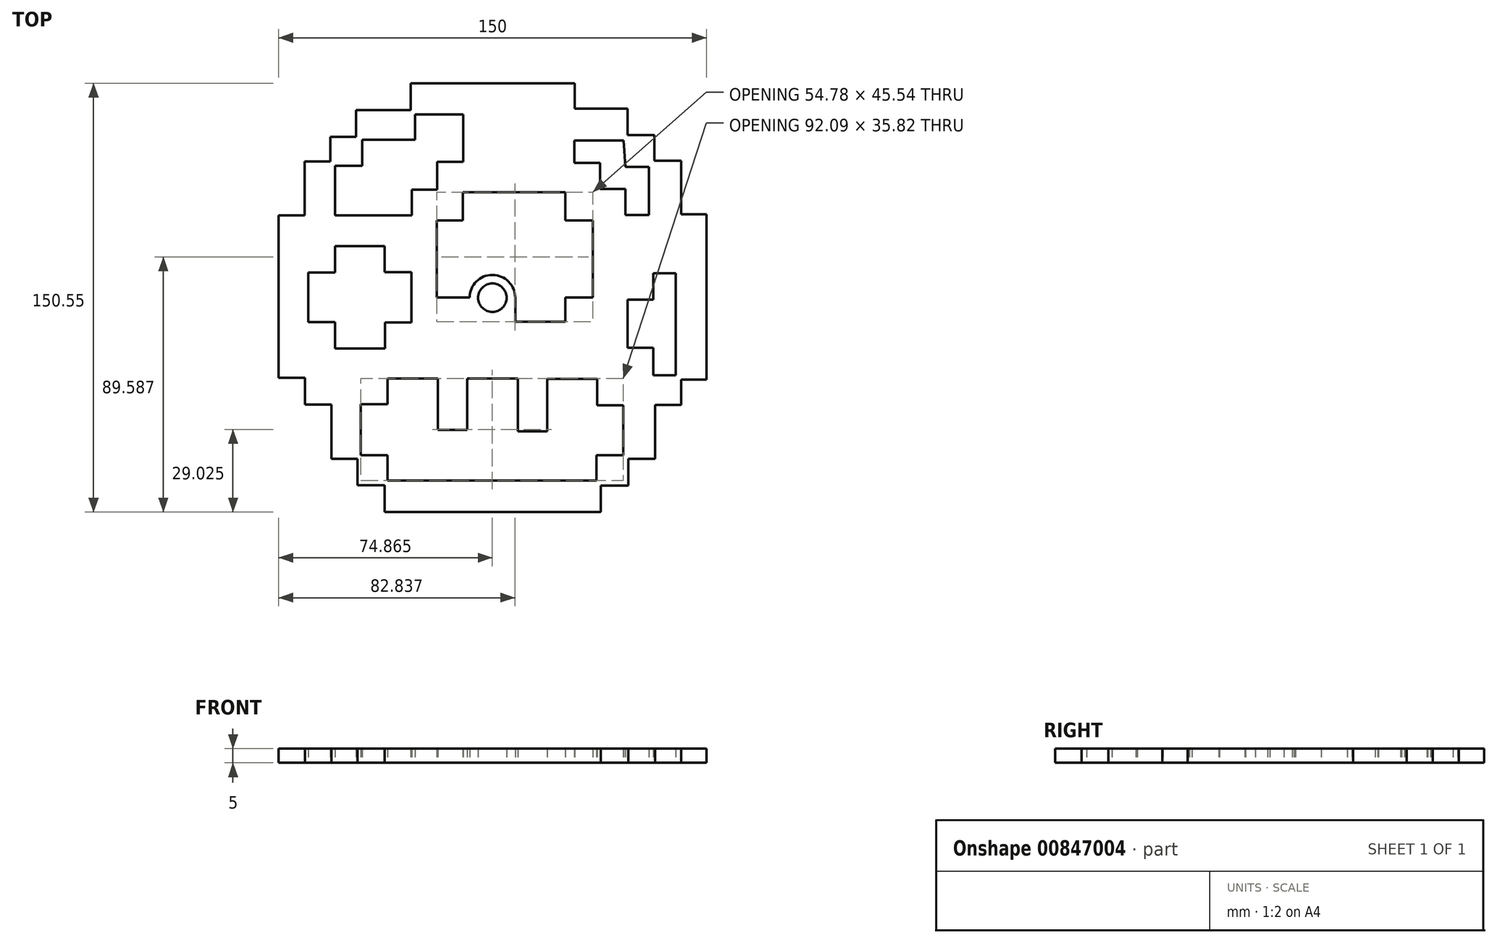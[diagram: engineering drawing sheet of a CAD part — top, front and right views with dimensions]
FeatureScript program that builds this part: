
annotation { "Feature Type Name" : "Feature", "Feature Type Description" : "" }
export const myFeature = defineFeature(function(context is Context, id is Id, definition is map)
    precondition{}
    {
        {
            var Q0;
            Q0=qCreatedBy(makeId("Top.planeOp"),FACE);
            var sketch = newSketch(context, id + "F0", { "sketchPlane" : qUnion([Q0])});
            skLineSegment(sketch, "E0", {"start": v(28.84, 75.26) * mm, "end": v(28.84, 66.32) * mm});
            skLineSegment(sketch, "E1", {"start": v(28.84, 66.32) * mm, "end": v(47.47, 66.32) * mm});
            skLineSegment(sketch, "E2", {"start": v(47.47, 66.32) * mm, "end": v(47.47, 57.16) * mm});
            skLineSegment(sketch, "E3", {"start": v(47.47, 57.16) * mm, "end": v(56.76, 57.16) * mm});
            skLineSegment(sketch, "E4", {"start": v(56.76, 57.16) * mm, "end": v(56.76, 48.02) * mm});
            skLineSegment(sketch, "E5", {"start": v(56.76, 48.02) * mm, "end": v(66.2, 48.02) * mm});
            skLineSegment(sketch, "E6", {"start": v(66.2, 48.02) * mm, "end": v(66.2, 29.31) * mm});
            skLineSegment(sketch, "E7", {"start": v(66.2, 29.31) * mm, "end": v(75.04, 29.31) * mm});
            skLineSegment(sketch, "E8", {"start": v(28.72, 55.17) * mm, "end": v(46.07, 55.17) * mm});
            skLineSegment(sketch, "E9", {"start": v(46.07, 55.17) * mm, "end": v(46.7, 45.9) * mm});
            skLineSegment(sketch, "E10", {"start": v(46.7, 45.9) * mm, "end": v(54.88, 45.9) * mm});
            skLineSegment(sketch, "E11", {"start": v(54.88, 45.9) * mm, "end": v(54.88, 29.09) * mm});
            skLineSegment(sketch, "E12", {"start": v(54.88, 29.09) * mm, "end": v(46.7, 29.09) * mm});
            skLineSegment(sketch, "E13", {"start": v(46.7, 29.09) * mm, "end": v(46.7, 38.14) * mm});
            skLineSegment(sketch, "E14", {"start": v(46.7, 38.14) * mm, "end": v(37.83, 38.14) * mm});
            skLineSegment(sketch, "E15", {"start": v(37.83, 38.14) * mm, "end": v(37.83, 47.34) * mm});
            skLineSegment(sketch, "E16", {"start": v(37.83, 47.34) * mm, "end": v(28.72, 47.34) * mm});
            skLineSegment(sketch, "E17", {"start": v(28.72, 47.34) * mm, "end": v(28.72, 55.17) * mm});
            skLineSegment(sketch, "E18.bottom", {"start": v(64.25, 8.55) * mm, "end": v(64.25, -27.21) * mm});
            skLineSegment(sketch, "E18.top", {"start": v(56.48, 8.55) * mm, "end": v(56.48, -0.68) * mm});
            skLineSegment(sketch, "E18.left", {"start": v(64.25, 8.55) * mm, "end": v(56.48, 8.55) * mm});
            skLineSegment(sketch, "E18.right", {"start": v(64.25, -27.21) * mm, "end": v(56.48, -27.21) * mm});
            skLineSegment(sketch, "E19.left", {"start": v(56.48, -17.53) * mm, "end": v(47.4, -17.53) * mm});
            skLineSegment(sketch, "E20.trimOffspring", {"start": v(56.48, -17.53) * mm, "end": v(56.48, -27.21) * mm});
            skLineSegment(sketch, "E21.bottom", {"start": v(35.27, 27.19) * mm, "end": v(35.27, 0.07) * mm});
            skLineSegment(sketch, "E21.top", {"start": v(-19.51, 27.19) * mm, "end": v(-19.51, 0.07) * mm});
            skLineSegment(sketch, "E22.left", {"start": v(-10.31, -8.47) * mm, "end": v(25.6, -8.47) * mm});
            skLineSegment(sketch, "E22.right", {"start": v(-10.31, 37.07) * mm, "end": v(25.6, 37.07) * mm});
            skLineSegment(sketch, "E23.bottom", {"start": v(-10.26, 64.31) * mm, "end": v(-10.26, 47.71) * mm});
            skLineSegment(sketch, "E23.left", {"start": v(-10.26, 64.31) * mm, "end": v(-27.16, 64.31) * mm});
            skLineSegment(sketch, "E24.top", {"start": v(-55.2, 28.94) * mm, "end": v(-55.2, 46.32) * mm});
            skLineSegment(sketch, "E24.left", {"start": v(-28.33, 28.94) * mm, "end": v(-55.2, 28.94) * mm});
            skLineSegment(sketch, "E25.bottom", {"start": v(-28.38, 9.02) * mm, "end": v(-28.38, -8.73) * mm});
            skLineSegment(sketch, "E25.top", {"start": v(-64.6, 8.78) * mm, "end": v(-64.6, -8.57) * mm});
            skLineSegment(sketch, "E26.left", {"start": v(-55.2, -17.88) * mm, "end": v(-37.61, -17.88) * mm});
            skLineSegment(sketch, "E26.right", {"start": v(-55.2, 18.09) * mm, "end": v(-37.77, 18.09) * mm});
            skLineSegment(sketch, "E27.left", {"start": v(36.72, -28.53) * mm, "end": v(19.26, -28.53) * mm});
            skLineSegment(sketch, "E28.top", {"start": v(45.95, -37.75) * mm, "end": v(45.95, -55.26) * mm});
            skLineSegment(sketch, "E28.left", {"start": v(36.72, -37.75) * mm, "end": v(45.95, -37.75) * mm});
            skLineSegment(sketch, "E28.right", {"start": v(36.5, -55.26) * mm, "end": v(45.95, -55.26) * mm});
            skLineSegment(sketch, "E29.bottom", {"start": v(8.9, -28.36) * mm, "end": v(8.9, -46.92) * mm});
            skLineSegment(sketch, "E29.top", {"start": v(-8.8, -28.36) * mm, "end": v(-8.8, -46.44) * mm});
            skLineSegment(sketch, "E29.left", {"start": v(8.9, -28.36) * mm, "end": v(-8.8, -28.36) * mm});
            skLineSegment(sketch, "E30.left", {"start": v(-36.74, -28.37) * mm, "end": v(-19.17, -28.37) * mm});
            skLineSegment(sketch, "E31.bottom", {"start": v(-46.14, -37.37) * mm, "end": v(-46.14, -55.28) * mm});
            skLineSegment(sketch, "E31.left", {"start": v(-46.14, -37.37) * mm, "end": v(-36.74, -37.37) * mm});
            skLineSegment(sketch, "E31.right", {"start": v(-46.14, -55.28) * mm, "end": v(-36.74, -55.28) * mm});
            skLineSegment(sketch, "E32.left", {"start": v(75.04, -28.78) * mm, "end": v(66.21, -28.78) * mm});
            skLineSegment(sketch, "E33.left", {"start": v(66.21, -37.61) * mm, "end": v(57.02, -37.61) * mm});
            skLineSegment(sketch, "E34.left", {"start": v(57.02, -56.53) * mm, "end": v(47.7, -56.53) * mm});
            skLineSegment(sketch, "E35.top", {"start": v(38.07, -65.97) * mm, "end": v(38.07, -75.3) * mm});
            skLineSegment(sketch, "E35.left", {"start": v(47.7, -65.97) * mm, "end": v(38.07, -65.97) * mm});
            skLineSegment(sketch, "E36.bottom", {"start": v(-37.76, -65.85) * mm, "end": v(-37.76, -75.3) * mm});
            skLineSegment(sketch, "E37.bottom", {"start": v(-47.3, -56.55) * mm, "end": v(-47.3, -65.85) * mm});
            skLineSegment(sketch, "E38.bottom", {"start": v(-56.4, -37.47) * mm, "end": v(-56.4, -56.55) * mm});
            skLineSegment(sketch, "E39.bottom", {"start": v(-65.7, -28.07) * mm, "end": v(-65.7, -37.47) * mm});
            skLineSegment(sketch, "E39.left", {"start": v(-65.7, -28.07) * mm, "end": v(-74.96, -28.07) * mm});
            skLineSegment(sketch, "E40.left", {"start": v(-74.96, 28.91) * mm, "end": v(-65.81, 28.91) * mm});
            skLineSegment(sketch, "E41.left", {"start": v(-65.81, 47.77) * mm, "end": v(-56.84, 47.77) * mm});
            skLineSegment(sketch, "E42.left", {"start": v(-56.84, 56.48) * mm, "end": v(-47.8, 56.48) * mm});
            skLineSegment(sketch, "E43.top", {"start": v(-28.63, 65.92) * mm, "end": v(-28.63, 75.26) * mm});
            skLineSegment(sketch, "E43.left", {"start": v(-47.8, 65.92) * mm, "end": v(-28.63, 65.92) * mm});
            skLineSegment(sketch, "E44", {"start": v(-19.51, 27.19) * mm, "end": v(-10.31, 27.19) * mm});
            skLineSegment(sketch, "E45", {"start": v(35.27, 27.19) * mm, "end": v(25.6, 27.19) * mm});
            skLineSegment(sketch, "E46", {"start": v(-19.51, 0.07) * mm, "end": v(-10.31, 0.07) * mm});
            skLineSegment(sketch, "E47", {"start": v(35.27, 0.07) * mm, "end": v(25.6, 0.07) * mm});
            skLineSegment(sketch, "E48", {"start": v(25.6, -8.47) * mm, "end": v(25.6, 0.07) * mm});
            skLineSegment(sketch, "E49", {"start": v(25.6, 27.19) * mm, "end": v(25.6, 37.07) * mm});
            skLineSegment(sketch, "E50", {"start": v(-10.31, 27.19) * mm, "end": v(-10.31, 37.07) * mm});
            skLineSegment(sketch, "E51", {"start": v(-10.31, 0.07) * mm, "end": v(-10.31, -8.47) * mm});
            skLineSegment(sketch, "E52", {"start": v(66.21, -28.78) * mm, "end": v(66.21, -37.61) * mm});
            skLineSegment(sketch, "E53", {"start": v(57.02, -37.61) * mm, "end": v(57.02, -56.53) * mm});
            skLineSegment(sketch, "E54", {"start": v(47.7, -56.53) * mm, "end": v(47.7, -65.97) * mm});
            skLineSegment(sketch, "E55", {"start": v(38.07, -75.3) * mm, "end": v(-37.76, -75.3) * mm});
            skLineSegment(sketch, "E56", {"start": v(-47.3, -65.85) * mm, "end": v(-37.76, -65.85) * mm});
            skLineSegment(sketch, "E57", {"start": v(-47.3, -56.55) * mm, "end": v(-56.4, -56.55) * mm});
            skLineSegment(sketch, "E58", {"start": v(-56.4, -37.47) * mm, "end": v(-65.7, -37.47) * mm});
            skLineSegment(sketch, "E59", {"start": v(-74.96, -28.07) * mm, "end": v(-74.96, 28.91) * mm});
            skLineSegment(sketch, "E60", {"start": v(-65.81, 28.91) * mm, "end": v(-65.81, 47.77) * mm});
            skLineSegment(sketch, "E61", {"start": v(-56.84, 47.77) * mm, "end": v(-56.84, 56.48) * mm});
            skLineSegment(sketch, "E62", {"start": v(-47.8, 56.48) * mm, "end": v(-47.8, 65.92) * mm});
            skLineSegment(sketch, "E63", {"start": v(-27.16, 64.31) * mm, "end": v(-27.16, 55.47) * mm});
            skLineSegment(sketch, "E64", {"start": v(-27.16, 55.47) * mm, "end": v(-45.66, 55.47) * mm});
            skLineSegment(sketch, "E65", {"start": v(-45.66, 55.47) * mm, "end": v(-45.66, 46.32) * mm});
            skLineSegment(sketch, "E66", {"start": v(-45.66, 46.32) * mm, "end": v(-55.2, 46.32) * mm});
            skLineSegment(sketch, "E67", {"start": v(-28.33, 28.94) * mm, "end": v(-28.33, 37.9) * mm});
            skLineSegment(sketch, "E68", {"start": v(-28.33, 37.9) * mm, "end": v(-19.32, 37.9) * mm});
            skLineSegment(sketch, "E69", {"start": v(-28.63, 75.26) * mm, "end": v(28.84, 75.26) * mm});
            skLineSegment(sketch, "E70", {"start": v(-37.77, 18.09) * mm, "end": v(-37.77, 9.02) * mm});
            skLineSegment(sketch, "E71", {"start": v(-37.77, 9.02) * mm, "end": v(-28.38, 9.02) * mm});
            skLineSegment(sketch, "E72", {"start": v(-28.38, -8.73) * mm, "end": v(-37.61, -8.73) * mm});
            skLineSegment(sketch, "E73", {"start": v(-37.61, -8.73) * mm, "end": v(-37.61, -17.88) * mm});
            skLineSegment(sketch, "E74", {"start": v(-55.2, -17.88) * mm, "end": v(-55.2, -8.57) * mm});
            skLineSegment(sketch, "E75", {"start": v(-64.6, -8.57) * mm, "end": v(-55.2, -8.57) * mm});
            skLineSegment(sketch, "E76", {"start": v(-64.6, 8.78) * mm, "end": v(-55.2, 8.78) * mm});
            skLineSegment(sketch, "E77", {"start": v(-55.2, 8.78) * mm, "end": v(-55.2, 18.09) * mm});
            skLineSegment(sketch, "E78", {"start": v(-36.74, -55.28) * mm, "end": v(-36.74, -64.17) * mm});
            skLineSegment(sketch, "E79", {"start": v(-36.74, -37.37) * mm, "end": v(-36.74, -28.37) * mm});
            skLineSegment(sketch, "E80", {"start": v(-19.17, -28.37) * mm, "end": v(-19.17, -46.44) * mm});
            skLineSegment(sketch, "E81", {"start": v(-19.17, -46.44) * mm, "end": v(-8.8, -46.44) * mm});
            skLineSegment(sketch, "E82", {"start": v(8.9, -46.92) * mm, "end": v(19.26, -46.92) * mm});
            skLineSegment(sketch, "E83", {"start": v(19.26, -46.92) * mm, "end": v(19.26, -28.53) * mm});
            skLineSegment(sketch, "E84", {"start": v(36.72, -28.53) * mm, "end": v(36.72, -37.75) * mm});
            skLineSegment(sketch, "E85", {"start": v(36.5, -55.26) * mm, "end": v(36.5, -64.17) * mm});
            skLineSegment(sketch, "E86", {"start": v(-36.74, -64.17) * mm, "end": v(36.5, -64.17) * mm});
            skLineSegment(sketch, "E87", {"start": v(75.04, 29.31) * mm, "end": v(75.04, -28.78) * mm});
            skLineSegment(sketch, "E88", {"start": v(56.48, -0.68) * mm, "end": v(47.47, -0.68) * mm});
            skLineSegment(sketch, "E89", {"start": v(47.47, -0.68) * mm, "end": v(47.4, -17.53) * mm});
            skLineSegment(sketch, "E90", {"start": v(-19.32, 37.9) * mm, "end": v(-19.32, 47.71) * mm});
            skLineSegment(sketch, "E91", {"start": v(-19.32, 47.71) * mm, "end": v(-10.26, 47.71) * mm});
            skCircle(sketch, "E92", {"center": v(0, 0) * mm, "radius": 8 * mm});
            skCircle(sketch, "E93.0", {"center": v(0, 0) * mm, "radius": 5 * mm});
            skLineSegment(sketch, "E94", {"start": v(-10.31, 0.07) * mm, "end": v(-8, 0.07) * mm});
            skLineSegment(sketch, "E95", {"start": v(8, 0) * mm, "end": v(8, -8.47) * mm});
            skPoint(sketch, "E96.center", {"position": v(1.03, 1.97) * mm});
            skSolve(sketch);
        }
        {
            var Q0;
            {var subQ47=sQuery(id+"F0.wireOp",EDGE,"E0");Q0=makeQuery(id+"F0.imprint","IMPRINT",FACE,{"disambiguationData":[TD([[makeQuery(id+"F0.imprint","IMPRINT",EDGE,{"derivedFrom":subQ47}),-1.0]])]});}
            var Q1;
            {var subQ5=sQuery(id+"F0.wireOp",EDGE,"E96.1.2");Q1=makeQuery(id+"F0.imprint","IMPRINT",FACE,{"disambiguationData":[TD([[makeQuery(id+"F0.imprint","IMPRINT",EDGE,{"derivedFrom":subQ5}),1.0]])]});}
            var Q2;
            {var subQ5=sQuery(id+"F0.wireOp",EDGE,"E96.1.0");Q2=makeQuery(id+"F0.imprint","IMPRINT",FACE,{"disambiguationData":[TD([[makeQuery(id+"F0.imprint","IMPRINT",EDGE,{"derivedFrom":subQ5}),-1.0]])]});}
            var Q3;
            {var subQ5=sQuery(id+"F0.wireOp",EDGE,"E96.2.2");Q3=makeQuery(id+"F0.imprint","IMPRINT",FACE,{"disambiguationData":[TD([[makeQuery(id+"F0.imprint","IMPRINT",EDGE,{"derivedFrom":subQ5}),1.0]])]});}
            var Q4;
            {var subQ5=sQuery(id+"F0.wireOp",EDGE,"E96.2.0");Q4=makeQuery(id+"F0.imprint","IMPRINT",FACE,{"disambiguationData":[TD([[makeQuery(id+"F0.imprint","IMPRINT",EDGE,{"derivedFrom":subQ5}),-1.0]])]});}
            var Q5;
            {var subQ5=sQuery(id+"F0.wireOp",EDGE,"E96.3.2");Q5=makeQuery(id+"F0.imprint","IMPRINT",FACE,{"disambiguationData":[TD([[makeQuery(id+"F0.imprint","IMPRINT",EDGE,{"derivedFrom":subQ5}),1.0]])]});}
            var Q6;
            {var subQ5=sQuery(id+"F0.wireOp",EDGE,"E96.3.0");Q6=makeQuery(id+"F0.imprint","IMPRINT",FACE,{"disambiguationData":[TD([[makeQuery(id+"F0.imprint","IMPRINT",EDGE,{"derivedFrom":subQ5}),-1.0]])]});}
            var Q7;
            {var subQ0=sQuery(id+"F0.wireOp",EDGE,"b5d18da8-e20b-45f5-a40c-556fc24cc88c.4.4.0");Q7=makeQuery(id+"F0.imprint","IMPRINT",FACE,{"disambiguationData":[TD([[makeQuery(id+"F0.imprint","IMPRINT",EDGE,{"derivedFrom":subQ0}),-1.0]])]});}
            var Q8;
            {var subQ0=sQuery(id+"F0.wireOp",EDGE,"b5d18da8-e20b-45f5-a40c-556fc24cc88c.6.4.0");Q8=makeQuery(id+"F0.imprint","IMPRINT",FACE,{"disambiguationData":[TD([[makeQuery(id+"F0.imprint","IMPRINT",EDGE,{"derivedFrom":subQ0}),1.0]])]});}
            var Q9;
            {var subQ0=sQuery(id+"F0.wireOp",EDGE,"b5d18da8-e20b-45f5-a40c-556fc24cc88c.6.5.0");Q9=makeQuery(id+"F0.imprint","IMPRINT",FACE,{"disambiguationData":[TD([[makeQuery(id+"F0.imprint","IMPRINT",EDGE,{"derivedFrom":subQ0}),1.0]])]});}
            var Q10;
            {var subQ0=sQuery(id+"F0.wireOp",EDGE,"E56");var subQ1=sQuery(id+"F0.wireOp",EDGE,"E36.bottom");var subQ2=makeQuery(id+"F0.imprint","INTERSECT",VERTEX,{"derivedFrom":[subQ1,subQ0]});Q10=makeQuery(id+"F0.imprint","IMPRINT",FACE,{"disambiguationData":[TD([[makeQuery(id+"F0.imprint","IMPRINT",EDGE,{"disambiguationData":[TD([[subQ2,-1.0]])],"derivedFrom":subQ1}),-1.0]])]});}
            var Q11;
            {var subQ5=sQuery(id+"F0.wireOp",EDGE,"b5d18da8-e20b-45f5-a40c-556fc24cc88c.4.6.0");Q11=makeQuery(id+"F0.imprint","IMPRINT",FACE,{"disambiguationData":[TD([[makeQuery(id+"F0.imprint","IMPRINT",EDGE,{"derivedFrom":subQ5}),-1.0]])]});}
            var Q12;
            {var subQ15=sQuery(id+"F0.wireOp",EDGE,"E35.top");Q12=makeQuery(id+"F0.imprint","IMPRINT",FACE,{"disambiguationData":[TD([[makeQuery(id+"F0.imprint","IMPRINT",EDGE,{"derivedFrom":subQ15}),-1.0]])]});}
            var Q13;
            {var subQ5=sQuery(id+"F0.wireOp",EDGE,"b5d18da8-e20b-45f5-a40c-556fc24cc88c.6.6.0");Q13=makeQuery(id+"F0.imprint","IMPRINT",FACE,{"disambiguationData":[TD([[makeQuery(id+"F0.imprint","IMPRINT",EDGE,{"derivedFrom":subQ5}),1.0]])]});}
            var Q14;
            {var subQ7=sQuery(id+"F0.wireOp",EDGE,"E56");var subQ8=sQuery(id+"F0.wireOp",EDGE,"E36.bottom");var subQ9=makeQuery(id+"F0.imprint","INTERSECT",VERTEX,{"derivedFrom":[subQ8,subQ7]});Q14=makeQuery(id+"F0.imprint","IMPRINT",FACE,{"disambiguationData":[TD([[makeQuery(id+"F0.imprint","IMPRINT",EDGE,{"disambiguationData":[TD([[subQ9,-1.0]])],"derivedFrom":subQ8}),1.0]])]});}
            var Q15;
            {var subQ3=sQuery(id+"F0.wireOp",EDGE,"E28.right");var subQ7=sQuery(id+"F0.wireOp",EDGE,"b5d18da8-e20b-45f5-a40c-556fc24cc88c.6.7.0");var subQ11=makeQuery(id+"F0.imprint","INTERSECT",VERTEX,{"derivedFrom":[subQ3,subQ7]});Q15=makeQuery(id+"F0.imprint","IMPRINT",FACE,{"disambiguationData":[TD([[makeQuery(id+"F0.imprint","IMPRINT",EDGE,{"disambiguationData":[TD([[subQ11,-1.0]])],"derivedFrom":subQ3}),-1.0]])]});}
            var Q16;
            {var subQ5=sQuery(id+"F0.wireOp",EDGE,"b5d18da8-e20b-45f5-a40c-556fc24cc88c.4.7.0");Q16=makeQuery(id+"F0.imprint","IMPRINT",FACE,{"disambiguationData":[TD([[makeQuery(id+"F0.imprint","IMPRINT",EDGE,{"derivedFrom":subQ5}),-1.0]])]});}
            var Q17;
            {var subQ5=sQuery(id+"F0.wireOp",EDGE,"b5d18da8-e20b-45f5-a40c-556fc24cc88c.4.8.0");Q17=makeQuery(id+"F0.imprint","IMPRINT",FACE,{"disambiguationData":[TD([[makeQuery(id+"F0.imprint","IMPRINT",EDGE,{"derivedFrom":subQ5}),-1.0]])]});}
            var Q18;
            {var subQ5=sQuery(id+"F0.wireOp",EDGE,"b5d18da8-e20b-45f5-a40c-556fc24cc88c.6.8.0");Q18=makeQuery(id+"F0.imprint","IMPRINT",FACE,{"disambiguationData":[TD([[makeQuery(id+"F0.imprint","IMPRINT",EDGE,{"derivedFrom":subQ5}),1.0]])]});}
            var Q19;
            {var subQ5=sQuery(id+"F0.wireOp",EDGE,"b5d18da8-e20b-45f5-a40c-556fc24cc88c.4.9.0");Q19=makeQuery(id+"F0.imprint","IMPRINT",FACE,{"disambiguationData":[TD([[makeQuery(id+"F0.imprint","IMPRINT",EDGE,{"derivedFrom":subQ5}),-1.0]])]});}
            var Q20;
            {var subQ5=sQuery(id+"F0.wireOp",EDGE,"b5d18da8-e20b-45f5-a40c-556fc24cc88c.6.9.0");Q20=makeQuery(id+"F0.imprint","IMPRINT",FACE,{"disambiguationData":[TD([[makeQuery(id+"F0.imprint","IMPRINT",EDGE,{"derivedFrom":subQ5}),1.0]])]});}
            var Q21;
            {var subQ5=sQuery(id+"F0.wireOp",EDGE,"b5d18da8-e20b-45f5-a40c-556fc24cc88c.4.10.0");Q21=makeQuery(id+"F0.imprint","IMPRINT",FACE,{"disambiguationData":[TD([[makeQuery(id+"F0.imprint","IMPRINT",EDGE,{"derivedFrom":subQ5}),-1.0]])]});}
            var Q22;
            {var subQ5=sQuery(id+"F0.wireOp",EDGE,"b5d18da8-e20b-45f5-a40c-556fc24cc88c.6.10.0");Q22=makeQuery(id+"F0.imprint","IMPRINT",FACE,{"disambiguationData":[TD([[makeQuery(id+"F0.imprint","IMPRINT",EDGE,{"derivedFrom":subQ5}),1.0]])]});}
            var Q23;
            Q23=makeQuery(id+"F0.imprint","IMPRINT",FACE,{"disambiguationData":[TD([[makeQuery(id+"F0.imprint","IMPRINT",EDGE,{"derivedFrom":sQuery(id+"F0.wireOp",EDGE,"E93.0")}),-1.0]])]});
            var Q24;
            {var subQ3=sQuery(id+"F0.wireOp",EDGE,"E51");Q24=makeQuery(id+"F0.imprint","IMPRINT",FACE,{"disambiguationData":[TD([[makeQuery(id+"F0.imprint","IMPRINT",EDGE,{"derivedFrom":subQ3}),1.0]])]});}
            var Q25;
            {var subQ5=sQuery(id+"F0.wireOp",EDGE,"b5d18da8-e20b-45f5-a40c-556fc24cc88c.6.11.0");Q25=makeQuery(id+"F0.imprint","IMPRINT",FACE,{"disambiguationData":[TD([[makeQuery(id+"F0.imprint","IMPRINT",EDGE,{"derivedFrom":subQ5}),1.0]])]});}
            var Q26;
            {var subQ5=sQuery(id+"F0.wireOp",EDGE,"b5d18da8-e20b-45f5-a40c-556fc24cc88c.4.11.0");Q26=makeQuery(id+"F0.imprint","IMPRINT",FACE,{"disambiguationData":[TD([[makeQuery(id+"F0.imprint","IMPRINT",EDGE,{"derivedFrom":subQ5}),-1.0]])]});}
            var Q27;
            {var subQ5=sQuery(id+"F0.wireOp",EDGE,"wVeoURK1-A0aP-YzeK-l84Z-mJ0T7iDMKsM6.bottom");Q27=makeQuery(id+"F0.imprint","IMPRINT",FACE,{"disambiguationData":[TD([[makeQuery(id+"F0.imprint","IMPRINT",EDGE,{"derivedFrom":subQ5}),1.0]])]});}
            var Q28;
            {var subQ5=sQuery(id+"F0.wireOp",EDGE,"wVeoURK1-A0aP-YzeK-l84Z-mJ0T7iDMKsM6.top");Q28=makeQuery(id+"F0.imprint","IMPRINT",FACE,{"disambiguationData":[TD([[makeQuery(id+"F0.imprint","IMPRINT",EDGE,{"derivedFrom":subQ5}),-1.0]])]});}
            var Q29;
            {var subQ0=sQuery(id+"F0.wireOp",EDGE,"E85");var subQ1=sQuery(id+"F0.wireOp",EDGE,"E28.right");var subQ2=makeQuery(id+"F0.imprint","INTERSECT",VERTEX,{"derivedFrom":[subQ1,subQ0]});Q29=makeQuery(id+"F0.imprint","IMPRINT",FACE,{"disambiguationData":[TD([[makeQuery(id+"F0.imprint","IMPRINT",EDGE,{"disambiguationData":[TD([[subQ2,-1.0]])],"derivedFrom":subQ1}),-1.0]])]});}
            extrude(context, id + "F1", {"entities" : qUnion([Q0, Q1, Q2, Q3, Q4, Q5, Q6, Q7, Q8, Q9, Q10, Q11, Q12, Q13, Q14, Q15, Q16, Q17, Q18, Q19, Q20, Q21, Q22, Q23, Q24, Q25, Q26, Q27, Q28, Q29]), "depth" : 5 * mm, "offsetDistance" : 25 * mm});
        }
    });
